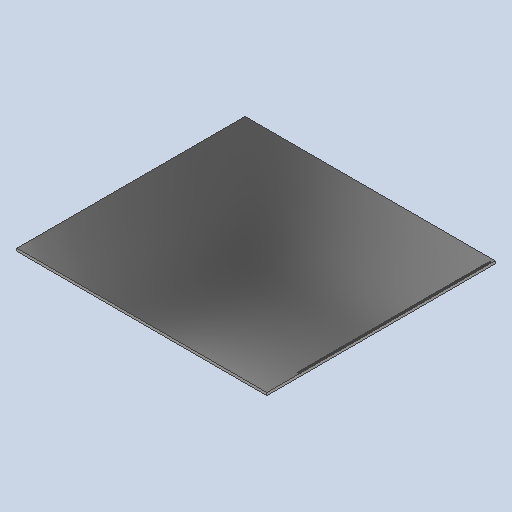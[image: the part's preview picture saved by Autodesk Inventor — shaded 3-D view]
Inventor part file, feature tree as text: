
AUTODESK INVENTOR PART (.ipt)
format: ipt  version: 2022 (Build 260153000, 153)  size: 824,320 bytes
history: native  units: in
note: dims shown in document units (in); Inventor stores cm internally (conversion verified against a paired STEP export)
features: sketch x3, extrude x2
ambient origin geometry x8: Origin, YZ Plane, XZ Plane, XY Plane, X Axis, Y Axis, Z Axis, Center Point
bodies: Solid1 (feature_tree)
feature tree (5):
  sketch  "Sketch1"  dims[d0=0.8268in d1=0.9055in]
  extrude  "Extrusion1"  Depth=0.9055in
  extrude  "Extrusion2"  Depth=0.0059in
  sketch  "Sketch2"  dims[d2=0.0098in d3=0.0in d4=0.0059in]
  sketch  "Sketch3"  dims[d5=0.0031in d6=55.9055in d8=0.0049in d9=0.3937in d11=0.3937in d13=0.1181in d14=0.002in d15=0.0264in d16=0.0004in d17=0.0in]
